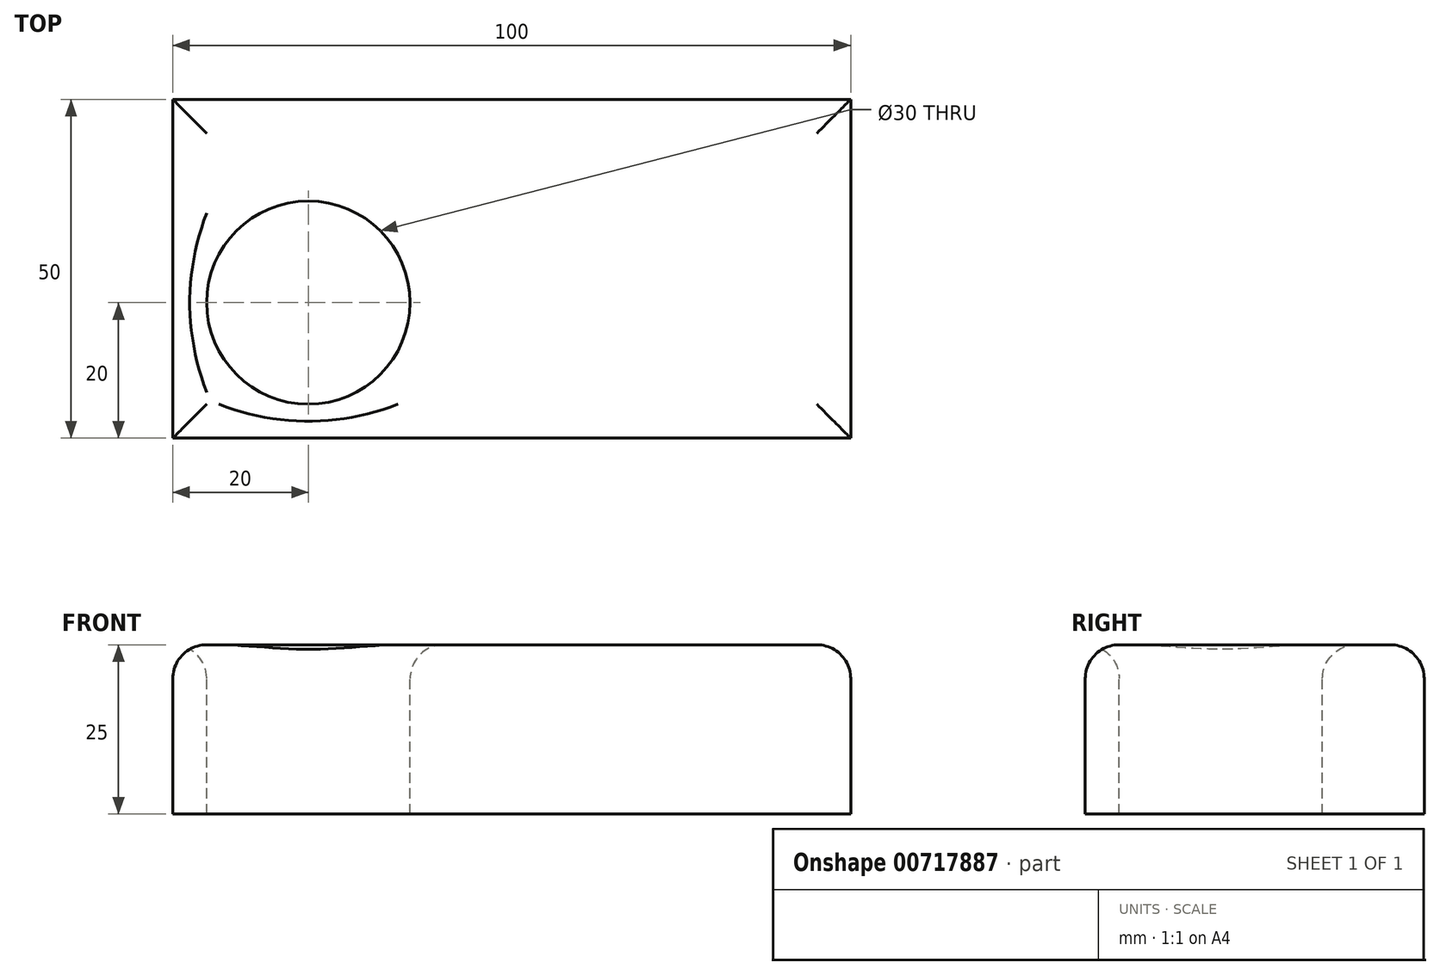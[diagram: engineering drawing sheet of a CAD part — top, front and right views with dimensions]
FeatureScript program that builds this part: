
annotation { "Feature Type Name" : "Feature", "Feature Type Description" : "" }
export const myFeature = defineFeature(function(context is Context, id is Id, definition is map)
    precondition{}
    {
        {
            var Q0;
            Q0=qCreatedBy(makeId("Top.planeOp"),FACE);
            var sketch = newSketch(context, id + "F0", { "sketchPlane" : qUnion([Q0])});
            skLineSegment(sketch, "E0.bottom", {"start": v(0, 0) * mm, "end": v(100, 0) * mm});
            skLineSegment(sketch, "E0.top", {"start": v(0, 50) * mm, "end": v(100, 50) * mm});
            skLineSegment(sketch, "E0.left", {"start": v(0, 0) * mm, "end": v(0, 50) * mm});
            skLineSegment(sketch, "E0.right", {"start": v(100, 0) * mm, "end": v(100, 50) * mm});
            skSolve(sketch);
        }
        {
            var Q0;
            Q0=makeQuery(id+"F0.imprint","IMPRINT",FACE,{"disambiguationData":[TD([[makeQuery(id+"F0.imprint","IMPRINT",EDGE,{"derivedFrom":sQuery(id+"F0.wireOp",EDGE,"E0.bottom")}),1.0]])]});
            extrude(context, id + "F1", {"entities" : qUnion([Q0]), "depth" : 25 * mm, "offsetDistance" : 25 * mm});
        }
        {
            var Q0;
            Q0=makeQuery(id+"F1.opExtrude","CAP_FACE",FACE,{"disambiguationData":[OSD([sQuery(id+"F0.wireOp",EDGE,"E0.bottom"),sQuery(id+"F0.wireOp",EDGE,"E0.top"),sQuery(id+"F0.wireOp",EDGE,"E0.left"),sQuery(id+"F0.wireOp",EDGE,"E0.right")])],"isStart":false});
            var sketch = newSketch(context, id + "F2", { "sketchPlane" : qUnion([Q0])});
            skCircle(sketch, "E1", {"center": v(20, 20) * mm, "radius": 15 * mm});
            skSolve(sketch);
        }
        {
            var Q0;
            Q0=makeQuery(id+"F2.imprint","IMPRINT",FACE,{"disambiguationData":[TD([[makeQuery(id+"F2.imprint","IMPRINT",EDGE,{"derivedFrom":sQuery(id+"F2.wireOp",EDGE,"E1")}),1.0]])]});
            extrude(context, id + "F3", {"entities" : qUnion([Q0]), "operationType" : NewBodyOperationType.REMOVE, "endBound" : BoundingType.THROUGH_ALL, "oppositeDirection" : true, "depth" : 25 * mm, "offsetDistance" : 25 * mm});
        }
        {
            var Q0;
            Q0=makeQuery(id+"F1.opExtrude","CAP_FACE",FACE,{"disambiguationData":[OSD([sQuery(id+"F0.wireOp",EDGE,"E0.bottom"),sQuery(id+"F0.wireOp",EDGE,"E0.top"),sQuery(id+"F0.wireOp",EDGE,"E0.left"),sQuery(id+"F0.wireOp",EDGE,"E0.right")])],"isStart":false});
            fillet(context, id + "F4", {"entities" : qUnion([Q0]), "radius" : 5 * mm, "tangentPropagation" : true, "allowEdgeOverflow" : false});
        }
    });
